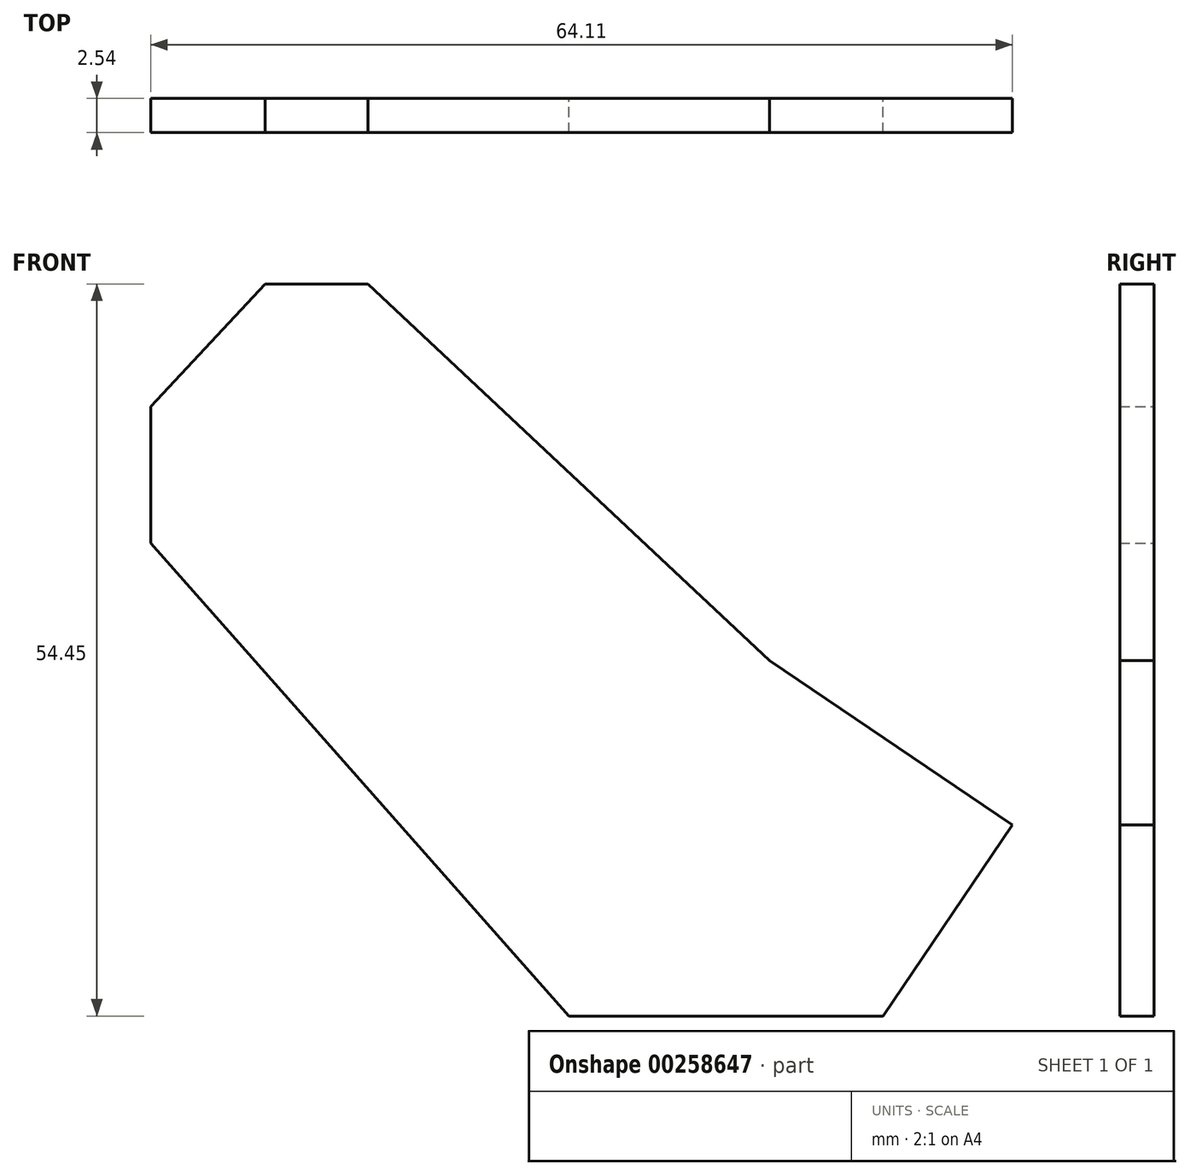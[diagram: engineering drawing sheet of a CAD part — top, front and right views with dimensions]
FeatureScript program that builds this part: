
annotation { "Feature Type Name" : "Feature", "Feature Type Description" : "" }
export const myFeature = defineFeature(function(context is Context, id is Id, definition is map)
    precondition{}
    {
        {
            var Q0;
            Q0=qCreatedBy(makeId("Front.planeOp"),FACE);
            var sketch = newSketch(context, id + "F0", { "sketchPlane" : qUnion([Q0])});
            skLineSegment(sketch, "E0", {"start": v(22, 12.24) * mm, "end": v(40.04, 0) * mm});
            skLineSegment(sketch, "E1", {"start": v(40.04, 0) * mm, "end": v(30.41, -14.2) * mm});
            skLineSegment(sketch, "E2", {"start": v(30.41, -14.2) * mm, "end": v(7.05, -14.2) * mm});
            skLineSegment(sketch, "E3", {"start": v(7.05, -14.2) * mm, "end": v(-24.07, 20.95) * mm});
            skLineSegment(sketch, "E4", {"start": v(-24.07, 20.95) * mm, "end": v(-24.07, 31.12) * mm});
            skLineSegment(sketch, "E5", {"start": v(-24.07, 31.12) * mm, "end": v(-15.56, 40.25) * mm});
            skLineSegment(sketch, "E6", {"start": v(-15.56, 40.25) * mm, "end": v(-7.88, 40.25) * mm});
            skLineSegment(sketch, "E7", {"start": v(-7.88, 40.25) * mm, "end": v(22, 12.24) * mm});
            skSolve(sketch);
        }
        {
            var Q0;
            Q0 = qSketchRegion(id + "F0", true);
            var Q1;
            Q1=makeQuery(id+"F0.imprint","IMPRINT",FACE,{"disambiguationData":[TD([[makeQuery(id+"F0.imprint","IMPRINT",EDGE,{"derivedFrom":sQuery(id+"F0.wireOp",EDGE,"E0")}),-1.0]])]});
            extrude(context, id + "F1", {"entities" : qUnion([Q0, Q1]), "depth" : 2.54 * mm});
        }
    });
